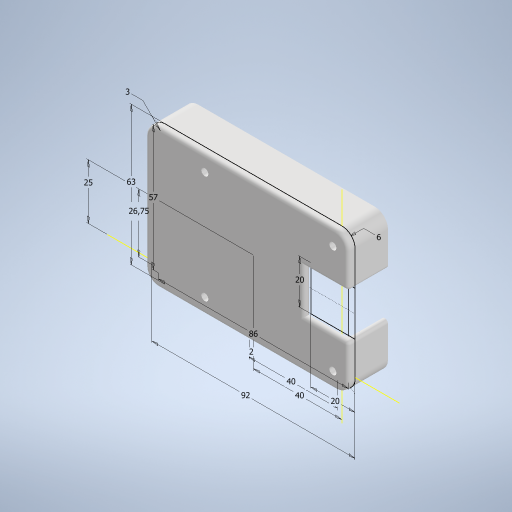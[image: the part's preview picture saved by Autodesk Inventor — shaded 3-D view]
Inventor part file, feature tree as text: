
AUTODESK INVENTOR PART (.ipt)
format: ipt  version: 2024.3 (Build 283343000, 343)  size: 414,208 bytes
history: native  units: in
note: dims shown in document units (in); Inventor stores cm internally (conversion verified against a paired STEP export)
features: extrude x4, sketch x2, fillet x1
ambient origin geometry x8: Origin, YZ Plane, XZ Plane, XY Plane, X Axis, Y Axis, Z Axis, Center Point
bodies: Solid1 (feature_tree)
feature tree (7):
  sketch  "Sketch1"  dims[d0=3.622in d1=2.4803in]
  extrude  "Extrusion1"  Depth=2.4803in
  sketch  "Sketch2"  dims[d2=0.9843in d3=1.5748in d5=0.1181in d6=0.0in d7=0.126in d8=1.9488in d9=0.126in d10=0.0197in d11=0.126in d12=2.2835in d13=0.126in d14=0.0394in d15=3.3858in d16=2.2441in d17=0.1181in d18=0.2362in d19=1.0531in d20=0.7874in d21=0.7874in d22=1.5748in d23=0.0787in d24=0.5906in d25=0.0in d26=0.0591in d27=0.2362in d28=0.2362in d29=0.2362in d30=0.2362in d31=0.1181in d32=0.0in d33=0.0in d34=0.0in]
  extrude  "Extrusion2"  Depth=0.1181in
  fillet  "Fillet1"  Radius=0.1181in
  extrude  "Extrusion3"  Depth=0.1181in
  extrude  "Extrusion4"  Depth=0.1181in
